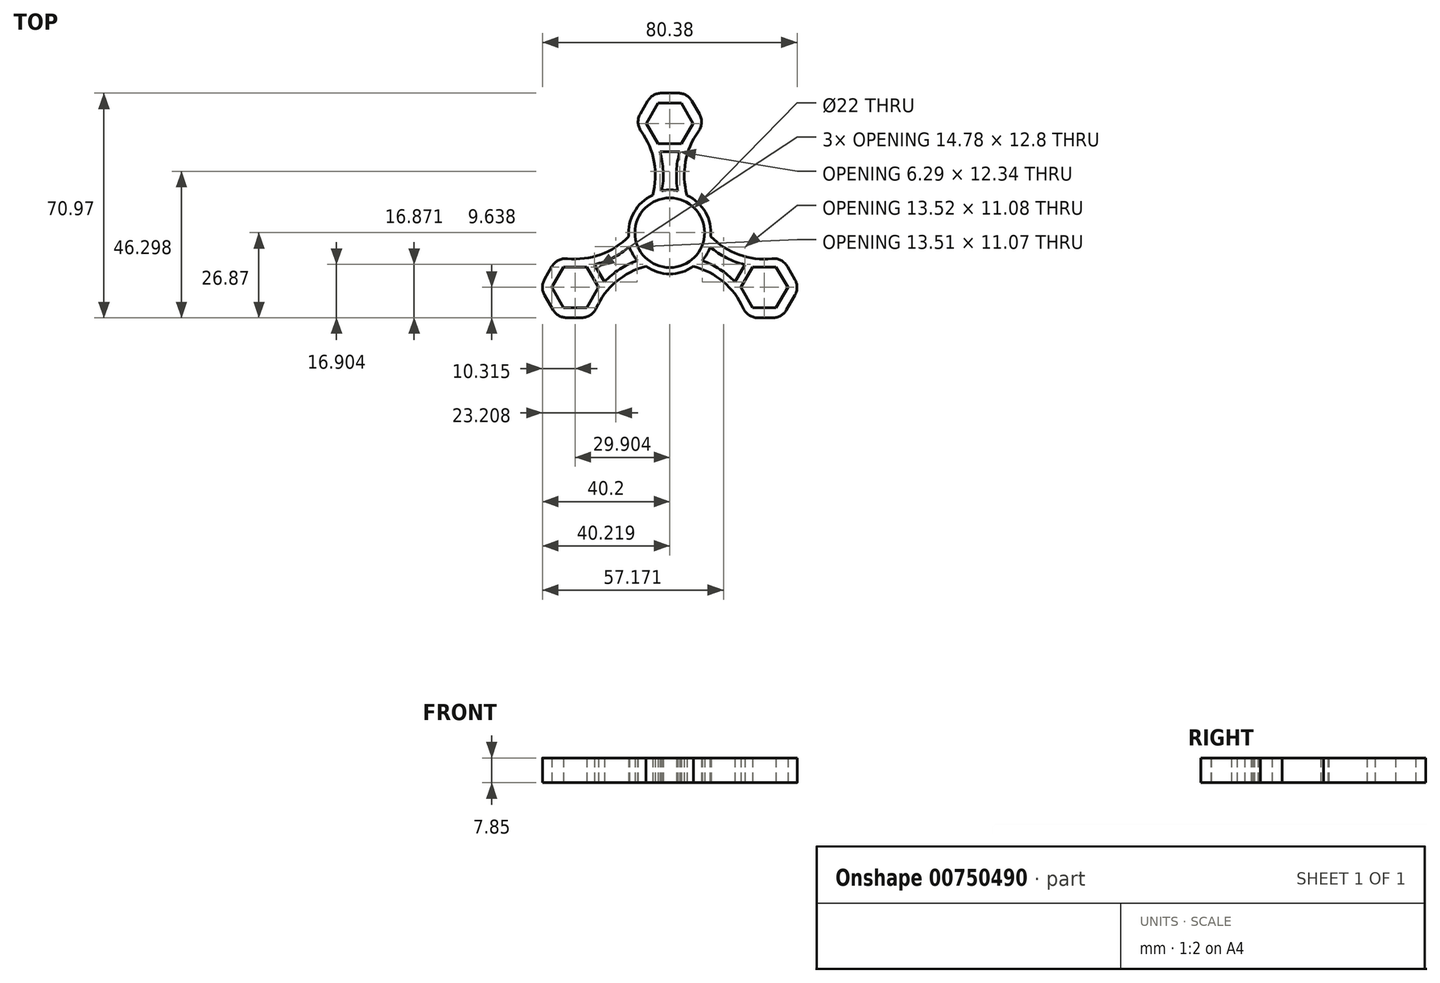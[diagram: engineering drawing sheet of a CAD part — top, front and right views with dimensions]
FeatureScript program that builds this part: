
annotation { "Feature Type Name" : "Feature", "Feature Type Description" : "" }
export const myFeature = defineFeature(function(context is Context, id is Id, definition is map)
    precondition{}
    {
        {
            var Q0;
            Q0=qCreatedBy(makeId("Top.planeOp"),FACE);
            var sketch = newSketch(context, id + "F0", { "sketchPlane" : qUnion([Q0])});
            skCircle(sketch, "E0", {"center": v(0, 0) * mm, "radius": 11 * mm});
            skCircle(sketch, "E1", {"center": v(0, 0) * mm, "radius": 13 * mm});
            skPoint(sketch, "E2.center", {"position": v(0.02, 0) * mm});
            skPoint(sketch, "E3.orphan", {"position": v(-13, 0) * mm});
            skCircle(sketch, "E4.cCircle", {"center": v(0.02, 34.5) * mm, "radius": 6.4 * mm, "construction": true});
            skLineSegment(sketch, "E4.0", {"start": v(3.71, 28.1) * mm, "end": v(-3.68, 28.1) * mm});
            skLineSegment(sketch, "E4.1", {"start": v(-3.68, 28.1) * mm, "end": v(-7.37, 34.5) * mm});
            skLineSegment(sketch, "E4.2", {"start": v(-7.37, 34.5) * mm, "end": v(-3.68, 40.9) * mm});
            skLineSegment(sketch, "E4.3", {"start": v(-3.68, 40.9) * mm, "end": v(3.71, 40.9) * mm});
            skLineSegment(sketch, "E4.4", {"start": v(3.71, 40.9) * mm, "end": v(7.4, 34.5) * mm});
            skLineSegment(sketch, "E4.5", {"start": v(7.4, 34.5) * mm, "end": v(3.71, 28.1) * mm});
            skPoint(sketch, "E4.0.midPoint", {"position": v(0.02, 28.1) * mm});
            skCircle(sketch, "E5.cCircle", {"center": v(0.02, 34.5) * mm, "radius": 9.6 * mm, "construction": true});
            skLineSegment(sketch, "E5.0", {"start": v(11.1, 34.5) * mm, "end": v(5.56, 24.9) * mm});
            skLineSegment(sketch, "E5.1", {"start": v(5.56, 24.9) * mm, "end": v(-5.52, 24.9) * mm});
            skLineSegment(sketch, "E5.2", {"start": v(-5.52, 24.9) * mm, "end": v(-11.07, 34.5) * mm});
            skLineSegment(sketch, "E5.3", {"start": v(-11.07, 34.5) * mm, "end": v(-5.52, 44.1) * mm});
            skLineSegment(sketch, "E5.4", {"start": v(-5.52, 44.1) * mm, "end": v(5.56, 44.1) * mm});
            skLineSegment(sketch, "E5.5", {"start": v(5.56, 44.1) * mm, "end": v(11.1, 34.5) * mm});
            skPoint(sketch, "E5.0.midPoint", {"position": v(8.33, 29.7) * mm});
            skArc(sketch, "E6", {"start": v(-13, 0) * mm, "mid": v(-4.58, 16.83) * mm, "end": v(-11.07, 34.5) * mm});
            skArc(sketch, "E7", {"start": v(11.1, 34.5) * mm, "mid": v(4.62, 16.84) * mm, "end": v(13, 0) * mm});
            skPoint(sketch, "E8.1.0", {"position": v(-24.34, -14.03) * mm});
            skLineSegment(sketch, "E8.1.1", {"start": v(-40.97, -17.23) * mm, "end": v(-35.43, -7.63) * mm});
            skPoint(sketch, "E8.1.2", {"position": v(6.5, -11.26) * mm});
            skArc(sketch, "E8.1.3", {"start": v(6.5, -11.26) * mm, "mid": v(-12.28, -12.39) * mm, "end": v(-24.34, -26.83) * mm});
            skLineSegment(sketch, "E8.1.4", {"start": v(-26.2, -10.83) * mm, "end": v(-22.5, -17.23) * mm});
            skLineSegment(sketch, "E8.1.5", {"start": v(-33.58, -10.83) * mm, "end": v(-26.2, -10.83) * mm});
            skCircle(sketch, "E8.1.6", {"center": v(-29.89, -17.23) * mm, "radius": 6.4 * mm, "construction": true});
            skLineSegment(sketch, "E8.1.7", {"start": v(-35.43, -26.83) * mm, "end": v(-40.97, -17.23) * mm});
            skLineSegment(sketch, "E8.1.8", {"start": v(-18.8, -17.23) * mm, "end": v(-24.34, -26.83) * mm});
            skLineSegment(sketch, "E8.1.9", {"start": v(-24.34, -26.83) * mm, "end": v(-35.43, -26.83) * mm});
            skPoint(sketch, "E8.1.10", {"position": v(-29.89, -7.63) * mm});
            skLineSegment(sketch, "E8.1.11", {"start": v(-26.2, -23.63) * mm, "end": v(-33.58, -23.63) * mm});
            skCircle(sketch, "E8.1.12", {"center": v(-29.89, -17.23) * mm, "radius": 9.6 * mm, "construction": true});
            skLineSegment(sketch, "E8.1.13", {"start": v(-22.5, -17.23) * mm, "end": v(-26.2, -23.63) * mm});
            skLineSegment(sketch, "E8.1.15", {"start": v(-35.43, -7.63) * mm, "end": v(-24.34, -7.63) * mm});
            skLineSegment(sketch, "E8.1.16", {"start": v(-37.28, -17.23) * mm, "end": v(-33.58, -10.83) * mm});
            skArc(sketch, "E8.1.17", {"start": v(-35.43, -7.63) * mm, "mid": v(-16.9, -4.42) * mm, "end": v(-6.5, 11.26) * mm});
            skLineSegment(sketch, "E8.1.18", {"start": v(-33.58, -23.63) * mm, "end": v(-37.28, -17.23) * mm});
            skLineSegment(sketch, "E8.1.19", {"start": v(-24.34, -7.63) * mm, "end": v(-18.8, -17.23) * mm});
            skPoint(sketch, "E8.1.21", {"position": v(0, 0.02) * mm});
            skPoint(sketch, "E8.2.0", {"position": v(24.32, -14.07) * mm});
            skLineSegment(sketch, "E8.2.1", {"start": v(35.4, -26.87) * mm, "end": v(24.32, -26.87) * mm});
            skPoint(sketch, "E8.2.2", {"position": v(6.5, 11.26) * mm});
            skArc(sketch, "E8.2.3", {"start": v(6.5, 11.26) * mm, "mid": v(16.87, -4.45) * mm, "end": v(35.4, -7.67) * mm});
            skLineSegment(sketch, "E8.2.4", {"start": v(22.48, -17.27) * mm, "end": v(26.17, -10.87) * mm});
            skLineSegment(sketch, "E8.2.5", {"start": v(26.17, -23.67) * mm, "end": v(22.48, -17.27) * mm});
            skCircle(sketch, "E8.2.6", {"center": v(29.87, -17.27) * mm, "radius": 6.4 * mm, "construction": true});
            skLineSegment(sketch, "E8.2.7", {"start": v(40.95, -17.27) * mm, "end": v(35.4, -26.87) * mm});
            skLineSegment(sketch, "E8.2.8", {"start": v(24.32, -7.67) * mm, "end": v(35.4, -7.67) * mm});
            skLineSegment(sketch, "E8.2.9", {"start": v(35.4, -7.67) * mm, "end": v(40.95, -17.27) * mm});
            skPoint(sketch, "E8.2.10", {"position": v(21.55, -22.07) * mm});
            skLineSegment(sketch, "E8.2.11", {"start": v(33.56, -10.87) * mm, "end": v(37.26, -17.27) * mm});
            skCircle(sketch, "E8.2.12", {"center": v(29.87, -17.27) * mm, "radius": 9.6 * mm, "construction": true});
            skLineSegment(sketch, "E8.2.13", {"start": v(26.17, -10.87) * mm, "end": v(33.56, -10.87) * mm});
            skLineSegment(sketch, "E8.2.15", {"start": v(24.32, -26.87) * mm, "end": v(18.78, -17.27) * mm});
            skLineSegment(sketch, "E8.2.16", {"start": v(33.56, -23.67) * mm, "end": v(26.17, -23.67) * mm});
            skArc(sketch, "E8.2.17", {"start": v(24.32, -26.87) * mm, "mid": v(12.28, -12.42) * mm, "end": v(-6.5, -11.26) * mm});
            skLineSegment(sketch, "E8.2.18", {"start": v(37.26, -17.27) * mm, "end": v(33.56, -23.67) * mm});
            skLineSegment(sketch, "E8.2.19", {"start": v(18.78, -17.27) * mm, "end": v(24.32, -7.67) * mm});
            skPoint(sketch, "E8.2.21", {"position": v(-0.01, -0.01) * mm});
            skSolve(sketch);
        }
        {
            var Q0;
            Q0=makeQuery(id+"F0.imprint","IMPRINT",FACE,{"disambiguationData":[TD([[makeQuery(id+"F0.imprint","IMPRINT",EDGE,{"derivedFrom":sQuery(id+"F0.wireOp",EDGE,"E1")}),-1.0]])]});
            var Q1;
            Q1=makeQuery(id+"F0.imprint","IMPRINT",FACE,{"disambiguationData":[TD([[makeQuery(id+"F0.imprint","IMPRINT",EDGE,{"derivedFrom":sQuery(id+"F0.wireOp",EDGE,"E0")}),-1.0]])]});
            var Q2;
            Q2=makeQuery(id+"F0.imprint","IMPRINT",FACE,{"disambiguationData":[TD([[makeQuery(id+"F0.imprint","IMPRINT",EDGE,{"derivedFrom":sQuery(id+"F0.wireOp",EDGE,"E4.0")}),1.0]])]});
            var Q3;
            {var subQ2=sQuery(id+"F0.wireOp",EDGE,"E8.2.1");Q3=makeQuery(id+"F0.imprint","IMPRINT",FACE,{"disambiguationData":[TD([[makeQuery(id+"F0.imprint","IMPRINT",EDGE,{"derivedFrom":subQ2}),-1.0]])]});}
            var Q4;
            {var subQ2=sQuery(id+"F0.wireOp",EDGE,"E8.1.1");Q4=makeQuery(id+"F0.imprint","IMPRINT",FACE,{"disambiguationData":[TD([[makeQuery(id+"F0.imprint","IMPRINT",EDGE,{"derivedFrom":subQ2}),-1.0]])]});}
            extrude(context, id + "F1", {"entities" : qUnion([Q0, Q1, Q2, Q3, Q4]), "depth" : 7.85 * mm, "offsetDistance" : 25 * mm});
        }
        {
            var Q0;
            Q0=makeQuery(id+"F1.opExtrude","CAP_FACE",FACE,{"disambiguationData":[OSD([sQuery(id+"F0.wireOp",EDGE,"E0"),sQuery(id+"F0.wireOp",EDGE,"E1"),sQuery(id+"F0.wireOp",EDGE,"E4.0"),sQuery(id+"F0.wireOp",EDGE,"E4.1"),sQuery(id+"F0.wireOp",EDGE,"E4.2"),sQuery(id+"F0.wireOp",EDGE,"E4.3"),sQuery(id+"F0.wireOp",EDGE,"E4.4"),sQuery(id+"F0.wireOp",EDGE,"E4.5"),sQuery(id+"F0.wireOp",EDGE,"E5.3"),sQuery(id+"F0.wireOp",EDGE,"E5.4"),sQuery(id+"F0.wireOp",EDGE,"E5.5"),sQuery(id+"F0.wireOp",EDGE,"E6"),sQuery(id+"F0.wireOp",EDGE,"E7"),sQuery(id+"F0.wireOp",EDGE,"E8.1.1"),sQuery(id+"F0.wireOp",EDGE,"E8.1.3"),sQuery(id+"F0.wireOp",EDGE,"E8.1.4"),sQuery(id+"F0.wireOp",EDGE,"E8.1.5"),sQuery(id+"F0.wireOp",EDGE,"E8.1.7"),sQuery(id+"F0.wireOp",EDGE,"E8.1.9"),sQuery(id+"F0.wireOp",EDGE,"E8.1.11"),sQuery(id+"F0.wireOp",EDGE,"E8.1.13"),sQuery(id+"F0.wireOp",EDGE,"E8.1.16"),sQuery(id+"F0.wireOp",EDGE,"E8.1.17"),sQuery(id+"F0.wireOp",EDGE,"E8.1.18"),sQuery(id+"F0.wireOp",EDGE,"E8.2.1"),sQuery(id+"F0.wireOp",EDGE,"E8.2.3"),sQuery(id+"F0.wireOp",EDGE,"E8.2.4"),sQuery(id+"F0.wireOp",EDGE,"E8.2.5"),sQuery(id+"F0.wireOp",EDGE,"E8.2.7"),sQuery(id+"F0.wireOp",EDGE,"E8.2.9"),sQuery(id+"F0.wireOp",EDGE,"E8.2.11"),sQuery(id+"F0.wireOp",EDGE,"E8.2.13"),sQuery(id+"F0.wireOp",EDGE,"E8.2.16"),sQuery(id+"F0.wireOp",EDGE,"E8.2.17"),sQuery(id+"F0.wireOp",EDGE,"E8.2.18")])],"isStart":false});
            var Q1;
            Q1=makeQuery(id+"F1.opExtrude","CAP_FACE",FACE,{"disambiguationData":[OSD([sQuery(id+"F0.wireOp",EDGE,"E0"),sQuery(id+"F0.wireOp",EDGE,"E1"),sQuery(id+"F0.wireOp",EDGE,"E4.0"),sQuery(id+"F0.wireOp",EDGE,"E4.1"),sQuery(id+"F0.wireOp",EDGE,"E4.2"),sQuery(id+"F0.wireOp",EDGE,"E4.3"),sQuery(id+"F0.wireOp",EDGE,"E4.4"),sQuery(id+"F0.wireOp",EDGE,"E4.5"),sQuery(id+"F0.wireOp",EDGE,"E5.3"),sQuery(id+"F0.wireOp",EDGE,"E5.4"),sQuery(id+"F0.wireOp",EDGE,"E5.5"),sQuery(id+"F0.wireOp",EDGE,"E6"),sQuery(id+"F0.wireOp",EDGE,"E7"),sQuery(id+"F0.wireOp",EDGE,"E8.1.1"),sQuery(id+"F0.wireOp",EDGE,"E8.1.3"),sQuery(id+"F0.wireOp",EDGE,"E8.1.4"),sQuery(id+"F0.wireOp",EDGE,"E8.1.5"),sQuery(id+"F0.wireOp",EDGE,"E8.1.7"),sQuery(id+"F0.wireOp",EDGE,"E8.1.9"),sQuery(id+"F0.wireOp",EDGE,"E8.1.11"),sQuery(id+"F0.wireOp",EDGE,"E8.1.13"),sQuery(id+"F0.wireOp",EDGE,"E8.1.16"),sQuery(id+"F0.wireOp",EDGE,"E8.1.17"),sQuery(id+"F0.wireOp",EDGE,"E8.1.18"),sQuery(id+"F0.wireOp",EDGE,"E8.2.1"),sQuery(id+"F0.wireOp",EDGE,"E8.2.3"),sQuery(id+"F0.wireOp",EDGE,"E8.2.4"),sQuery(id+"F0.wireOp",EDGE,"E8.2.5"),sQuery(id+"F0.wireOp",EDGE,"E8.2.7"),sQuery(id+"F0.wireOp",EDGE,"E8.2.9"),sQuery(id+"F0.wireOp",EDGE,"E8.2.11"),sQuery(id+"F0.wireOp",EDGE,"E8.2.13"),sQuery(id+"F0.wireOp",EDGE,"E8.2.16"),sQuery(id+"F0.wireOp",EDGE,"E8.2.17"),sQuery(id+"F0.wireOp",EDGE,"E8.2.18")])],"isStart":true});
            shell(context, id + "F2", {"entities" : qUnion([Q0, Q1]), "thickness" : 2.5 * mm});
        }
        {
            var Q0;
            Q0=makeQuery(id+"F1.opExtrude","SWEPT_EDGE",EDGE,{"disambiguationData":[OSD([sQuery(id+"F0.wireOp",EDGE,"E8.1.1"),sQuery(id+"F0.wireOp",EDGE,"E8.1.15"),sQuery(id+"F0.wireOp",EDGE,"E8.1.17")])]});
            var Q1;
            Q1=makeQuery(id+"F1.opExtrude","SWEPT_EDGE",EDGE,{"disambiguationData":[OSD([sQuery(id+"F0.wireOp",EDGE,"E8.1.3"),sQuery(id+"F0.wireOp",EDGE,"E8.1.8"),sQuery(id+"F0.wireOp",EDGE,"E8.1.9")])]});
            var Q2;
            Q2=makeQuery(id+"F1.opExtrude","SWEPT_EDGE",EDGE,{"disambiguationData":[OSD([sQuery(id+"F0.wireOp",EDGE,"E5.0"),sQuery(id+"F0.wireOp",EDGE,"E5.5"),sQuery(id+"F0.wireOp",EDGE,"E7")])]});
            var Q3;
            Q3=makeQuery(id+"F1.opExtrude","SWEPT_EDGE",EDGE,{"disambiguationData":[OSD([sQuery(id+"F0.wireOp",EDGE,"E5.3"),sQuery(id+"F0.wireOp",EDGE,"E5.4")])]});
            var Q4;
            Q4=makeQuery(id+"F1.opExtrude","SWEPT_EDGE",EDGE,{"disambiguationData":[OSD([sQuery(id+"F0.wireOp",EDGE,"E5.2"),sQuery(id+"F0.wireOp",EDGE,"E5.3"),sQuery(id+"F0.wireOp",EDGE,"E6")])]});
            var Q5;
            Q5=makeQuery(id+"F1.opExtrude","SWEPT_EDGE",EDGE,{"disambiguationData":[OSD([sQuery(id+"F0.wireOp",EDGE,"E5.4"),sQuery(id+"F0.wireOp",EDGE,"E5.5")])]});
            var Q6;
            Q6=makeQuery(id+"F1.opExtrude","SWEPT_EDGE",EDGE,{"disambiguationData":[OSD([sQuery(id+"F0.wireOp",EDGE,"E8.2.7"),sQuery(id+"F0.wireOp",EDGE,"E8.2.9")])]});
            var Q7;
            Q7=makeQuery(id+"F1.opExtrude","SWEPT_EDGE",EDGE,{"disambiguationData":[OSD([sQuery(id+"F0.wireOp",EDGE,"E8.2.1"),sQuery(id+"F0.wireOp",EDGE,"E8.2.7")])]});
            var Q8;
            Q8=makeQuery(id+"F1.opExtrude","SWEPT_EDGE",EDGE,{"disambiguationData":[OSD([sQuery(id+"F0.wireOp",EDGE,"E8.2.1"),sQuery(id+"F0.wireOp",EDGE,"E8.2.15"),sQuery(id+"F0.wireOp",EDGE,"E8.2.17")])]});
            var Q9;
            Q9=makeQuery(id+"F1.opExtrude","SWEPT_EDGE",EDGE,{"disambiguationData":[OSD([sQuery(id+"F0.wireOp",EDGE,"E8.2.3"),sQuery(id+"F0.wireOp",EDGE,"E8.2.8"),sQuery(id+"F0.wireOp",EDGE,"E8.2.9")])]});
            var Q10;
            Q10=makeQuery(id+"F1.opExtrude","SWEPT_EDGE",EDGE,{"disambiguationData":[OSD([sQuery(id+"F0.wireOp",EDGE,"E8.1.1"),sQuery(id+"F0.wireOp",EDGE,"E8.1.7")])]});
            var Q11;
            Q11=makeQuery(id+"F1.opExtrude","SWEPT_EDGE",EDGE,{"disambiguationData":[OSD([sQuery(id+"F0.wireOp",EDGE,"E8.1.7"),sQuery(id+"F0.wireOp",EDGE,"E8.1.9")])]});
            fillet(context, id + "F3", {"entities" : qUnion([Q0, Q1, Q2, Q3, Q4, Q5, Q6, Q7, Q8, Q9, Q10, Q11]), "radius" : 5 * mm, "tangentPropagation" : true, "allowEdgeOverflow" : false});
        }
    });
